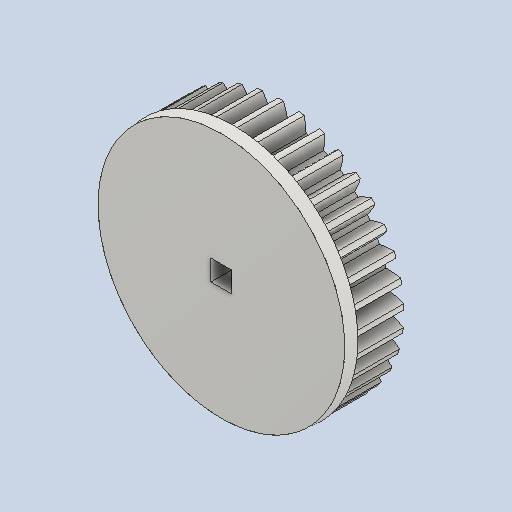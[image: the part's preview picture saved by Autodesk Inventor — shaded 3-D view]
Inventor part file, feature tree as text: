
AUTODESK INVENTOR PART (.ipt)
format: ipt  version: 2022 (Build 260153000, 153)  size: 1,346,560 bytes
history: native  units: mm (DEFAULTED — no unit token found)
features: sketch x4, extrude x3, plane x3, other x3, chamfer x1, revolve x1, projected_geometry x1
ambient origin geometry x8: Origin, YZ Plane, XZ Plane, XY Plane, X Axis, Y Axis, Z Axis, Center Point
bodies: Solid1 (feature_tree)
feature tree (16):
  extrude  "Extrusion1"  Depth=9.525mm TaperAngle=0.0deg
  plane  "Work Plane1"
  plane  "Work Plane2"
  plane  "Work Plane3"
  other  "Spur Gear"
  extrude  "Extrusion2"  Depth=76.2mm TaperAngle=0.0deg
  extrude  "Extrusion3"  TaperAngle=0.0deg  [1 undecoded]
  chamfer  "Chamfer1"  Distance=23.75408mm
  revolve  "Revolution1"  [1 undecoded]
  sketch  "Sketch1"  dims[d0=39.50816mm d1=9.525mm d2=0.0mm]
  sketch  "Sketch2"  dims[d3=37.0mm d4=76.2mm d5=0.0mm]
  other  "Srf1"
  sketch  "Sketch3"  dims[d6=0.0mm d7=0.849079mm d9=0.0mm]
  sketch  "Sketch4"  dims[d14=0.0mm d15=23.75408mm d16=0.0mm d17=0.0mm d18=0.0mm d19=23.75408mm d20=3.325mm d21=0.0mm d22=0.0mm d23=12.1mm d24=1.5875mm d25=0.0mm d26=1.5875mm d27=3.175mm d28=45.0deg d29=35.0mm d30=6.35mm d32=9.525mm d33=39.5mm d34=360.0deg d35=1.2mm d36=14.835299mm]
  projected_geometry  "Projected Loop1"
  other  "Pitch Diameter"
note: 2 required parameter values undecoded (feature->parameter linkage not recoverable at this tier; creation-order binding heuristic only, values carry confidence <= 0.55)